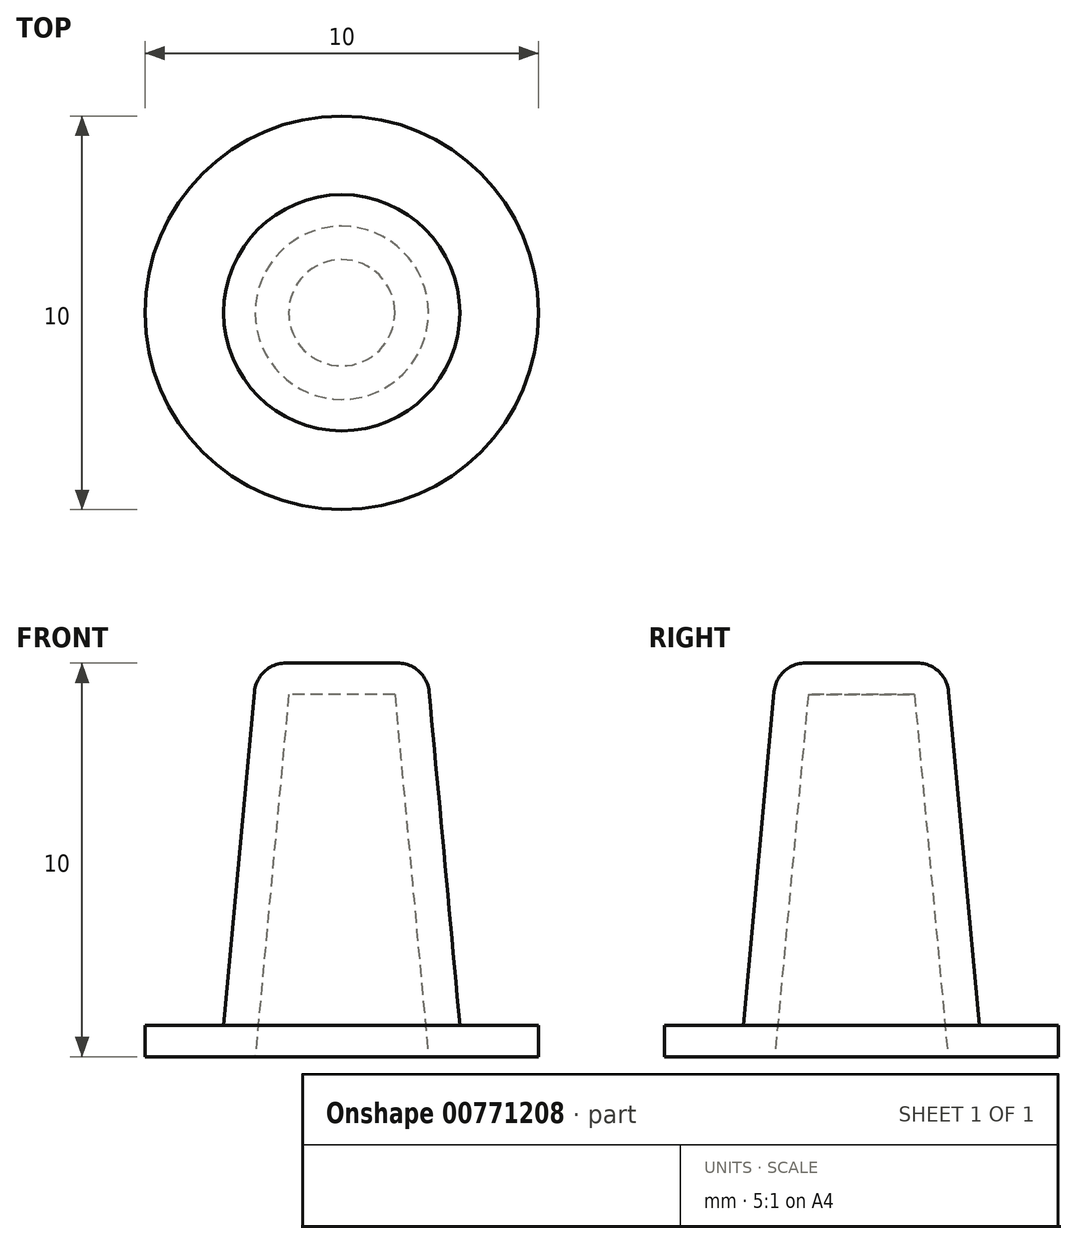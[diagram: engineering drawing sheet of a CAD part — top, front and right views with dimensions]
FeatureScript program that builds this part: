
annotation { "Feature Type Name" : "Feature", "Feature Type Description" : "" }
export const myFeature = defineFeature(function(context is Context, id is Id, definition is map)
    precondition{}
    {
        {
            var Q0;
            Q0=qCreatedBy(makeId("Front.planeOp"),FACE);
            var sketch = newSketch(context, id + "F0", { "sketchPlane" : qUnion([Q0])});
            skLineSegment(sketch, "E0", {"start": v(5, 0) * mm, "end": v(5, 0.8) * mm});
            skLineSegment(sketch, "E1", {"start": v(5, 0.8) * mm, "end": v(3, 0.8) * mm});
            skLineSegment(sketch, "E2", {"start": v(3, 0.8) * mm, "end": v(2.15, 10) * mm});
            skLineSegment(sketch, "E3", {"start": v(2.15, 10) * mm, "end": v(0, 10) * mm});
            skLineSegment(sketch, "E4", {"start": v(5, 0) * mm, "end": v(2.2, 0) * mm});
            skLineSegment(sketch, "E5", {"start": v(2.2, 0) * mm, "end": v(1.35, 9.2) * mm});
            skLineSegment(sketch, "E6", {"start": v(1.35, 9.2) * mm, "end": v(0, 9.2) * mm});
            skLineSegment(sketch, "E7", {"start": v(0, 9.2) * mm, "end": v(0, 10) * mm});
            skLineSegment(sketch, "E8", {"start": v(0, 17.92) * mm, "end": v(0, -8.43) * mm, "construction": true});
            skSolve(sketch);
        }
        {
            var Q0;
            Q0 = qSketchRegion(id + "F0", true);
            var Q1;
            Q1=sQuery(id+"F0.wireOp",EDGE,"E8");
            revolve(context, id + "F1", {"surfaceOperationType" : NewSurfaceOperationType.NEW, "entities" : qUnion([Q0]), "axis" : qUnion([Q1]), "revolveType" : RevolveType.FULL});
        }
        {
            var Q0;
            Q0=makeQuery(id+"F1.opRevolve","SWEPT_EDGE",EDGE,{"disambiguationData":[OSD([sQuery(id+"F0.wireOp",EDGE,"E2"),sQuery(id+"F0.wireOp",EDGE,"E3")])]});
            fillet(context, id + "F2", {"entities" : qUnion([Q0]), "radius" : 0.8 * mm, "tangentPropagation" : true, "allowEdgeOverflow" : false});
        }
    });
